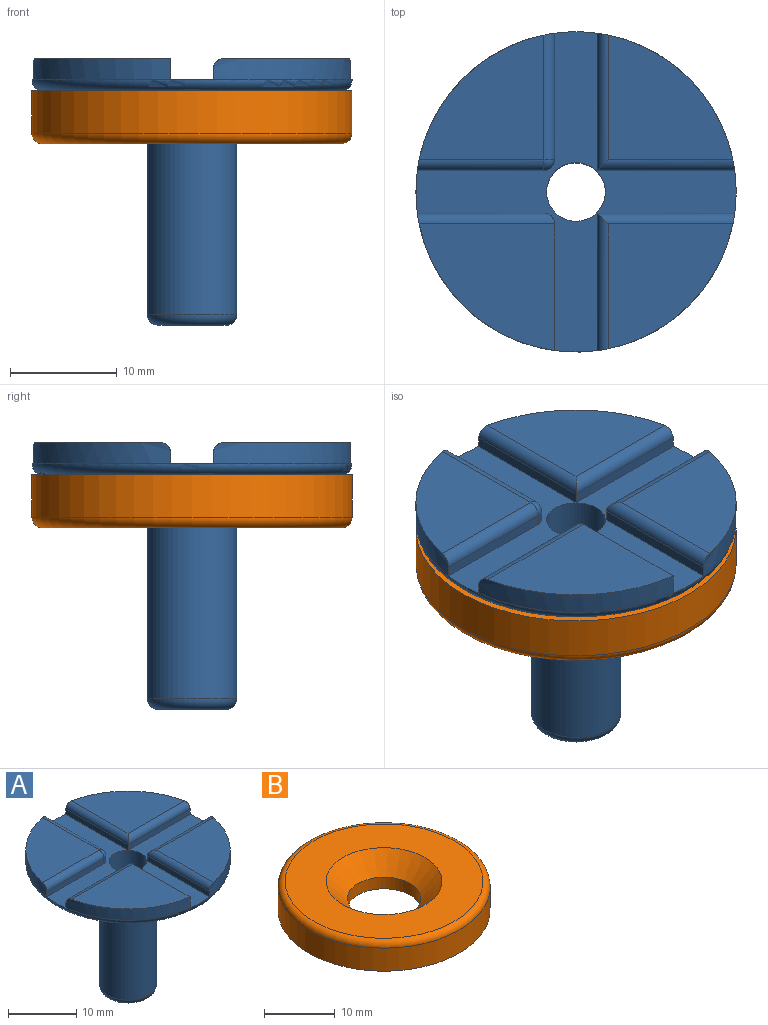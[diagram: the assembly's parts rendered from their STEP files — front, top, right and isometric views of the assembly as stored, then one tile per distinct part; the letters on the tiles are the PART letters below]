
ASSEMBLY  parts=2 mates=1
PART A: 37 faces, bbox 32.5x32.5x25 mm
  f0: cylinder r=15mm len=12.87mm, axis (0,0,1), area 38.7mm2, adj f7,f18,f19,f31,f32,f36
  f1: cylinder r=15mm len=12.87mm, axis (0,0,1), area 38.7mm2, adj f11,f20,f21,f25,f26,f36
  f2: cylinder r=15mm len=12.87mm, axis (0,0,1), area 38.9mm2, adj f9,f15,f22,f29,f36
  f3: plane 23x23mm, normal (0,0,-1), area 238.8mm2, adj f23,f24
  f4: plane 13x13mm, normal (0,0,-1), area 77.3mm2, adj f12,f24
  f5: plane 28x28mm, normal (0,0,-1), area 124.9mm2, adj f23,f36
  f6: cylinder r=15mm len=12.87mm, axis (0,0,1), area 38.7mm2, adj f8,f16,f17,f33,f34,f36
  f7: plane 11.7x11.7mm, normal (0,0,1), area 96.3mm2, adj f0,f31,f32
  f8: plane 11.7x11.7mm, normal (0,0,1), area 96.3mm2, adj f6,f33,f34
  f9: plane 12.7x11.87mm, normal (0,0,1), area 108.1mm2, adj f2,f15,f29
  f10: cylinder r=2.75mm len=23mm, axis (0,0,1), area 397.4mm2, adj f13,f14
  f11: plane 11.7x11.7mm, normal (0,0,1), area 96.3mm2, adj f1,f25,f26
  f12: cylinder r=4.2mm len=21mm, axis (0,0,1), area 554.2mm2, adj f4,f35
  f13: plane 6.4x6.4mm, normal (0,0,-1), area 8.4mm2, adj f10,f35
  f14: plane 30x30mm, normal (0,0,1), area 200mm2, adj f10,f15,f16,f17,f18,f19,f20,f21
  f15: plane 11.87x2mm, normal (1,0,0), area 23.7mm2, adj f2,f9,f14,f30
  f16: plane 12.87x1mm, normal (-1,0,0), area 12.9mm2, adj f6,f14,f17,f33
  f17: plane 12.87x1mm, normal (0,1,0), area 12.9mm2, adj f6,f14,f16,f34
  f18: plane 12.87x1mm, normal (0,-1,0), area 12.9mm2, adj f0,f14,f19,f31
  f19: plane 12.87x1mm, normal (-1,0,0), area 12.9mm2, adj f0,f14,f18,f32
  f20: plane 11.87x1mm, normal (1,0,0), area 11.9mm2, adj f1,f14,f26,f28
  f21: plane 11.87x1mm, normal (0,-1,0), area 11.9mm2, adj f1,f14,f25,f28
  f22: plane 11.87x1mm, normal (0,1,0), area 11.9mm2, adj f2,f14,f29,f30
  f23: torus R=12mm, axis (0,0,-1), area 122mm2, adj f3,f5
  f24: torus R=7mm, axis (0,0,-1), area 71.2mm2, adj f3,f4
  f25: cylinder r=1mm len=11.87mm, axis (1,0,0), area 18.6mm2, adj f1,f11,f21,f27
  f26: cylinder r=1mm len=11.87mm, axis (0,1,0), area 18.6mm2, adj f1,f11,f20,f27
  f27: sphere r=1mm, area 1.6mm2, adj f25,f26,f28
  f28: cylinder r=1mm len=1mm, axis (0,0,1), area 1.6mm2, adj f14,f20,f21,f27
  f29: cylinder r=1mm len=12.87mm, axis (-1,0,0), area 19.6mm2, adj f2,f9,f22,f30
  f30: cylinder r=1mm len=2mm, axis (0,0,1), area 2.6mm2, adj f14,f15,f22,f29
  f31: cylinder r=1mm len=12.87mm, axis (1,0,0), area 19.6mm2, adj f0,f7,f18,f32
  f32: cylinder r=1mm len=12.87mm, axis (0,-1,0), area 19.6mm2, adj f0,f7,f19,f31
  f33: cylinder r=1mm len=12.87mm, axis (0,-1,0), area 19.6mm2, adj f6,f8,f16,f34
  f34: cylinder r=1mm len=12.87mm, axis (-1,0,0), area 19.6mm2, adj f6,f8,f17,f33
  f35: torus R=3.2mm, axis (0,0,1), area 37.9mm2, adj f12,f13
  f36: torus R=14mm, axis (0,0,1), area 144.5mm2, adj f0,f1,f2,f5,f6,f14
PART B: 10 faces, bbox 32.5x32.5x5.4 mm
  f0: plane 13x13mm, normal (0,0,-1), area 47.8mm2, adj f2,f7
  f1: plane 30x30mm, normal (0,0,-1), area 216mm2, adj f3,f6
  f2: cylinder r=5.2mm len=10.4mm, axis (0,0,-1), area 65.3mm2, adj f0,f5
  f3: cylinder r=15mm len=30mm, axis (0,0,-1), area 377mm2, adj f1,f9
  f4: plane 28x28mm, normal (0,0,1), area 404.5mm2, adj f5,f9
  f5: cone r=5.2mm half-angle=45deg, axis (0,0,1), area 178.6mm2, adj f2,f4
  f6: torus R=12mm, axis (0,0,1), area 118.4mm2, adj f1,f8
  f7: torus R=7mm, axis (0,0,1), area 69.1mm2, adj f0,f8
  f8: plane 23x23mm, normal (0,0,-1), area 238.8mm2, adj f6,f7
  f9: torus R=14mm, axis (0,0,1), area 144.5mm2, adj f3,f4
PLACE A t=(21.89,1.53,-8.65)mm
PLACE B rot(axis=(0,1,0),180deg) t=(21.89,1.53,-11.65)mm
MATE fastened A.f12 <-> B.f2  axis (0,0,-1) through (21.89,1.53,-11.65)mm
